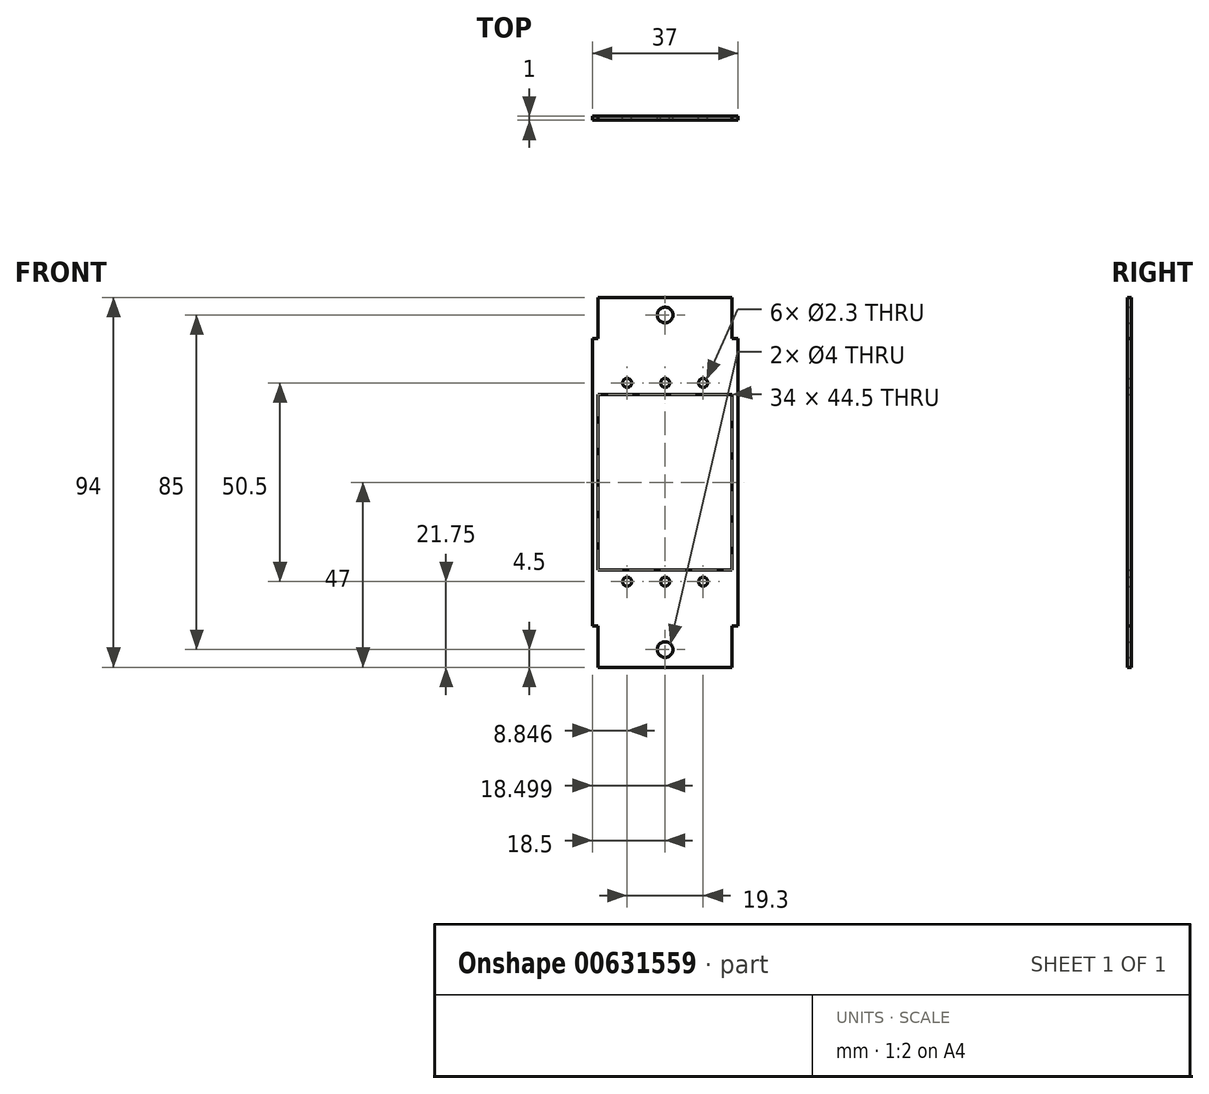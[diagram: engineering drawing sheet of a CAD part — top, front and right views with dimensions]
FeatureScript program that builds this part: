
annotation { "Feature Type Name" : "Feature", "Feature Type Description" : "" }
export const myFeature = defineFeature(function(context is Context, id is Id, definition is map)
    precondition{}
    {
        {
            var Q0;
            Q0=qCreatedBy(makeId("Front.planeOp"),FACE);
            var sketch = newSketch(context, id + "F0", { "sketchPlane" : qUnion([Q0])});
            skLineSegment(sketch, "E0.bottom", {"start": v(-17, 47) * mm, "end": v(17, 47) * mm});
            skLineSegment(sketch, "E0.top", {"start": v(-17, -47) * mm, "end": v(17, -47) * mm});
            skLineSegment(sketch, "E0.left", {"start": v(-18.5, 36.5) * mm, "end": v(-18.5, -36.5) * mm});
            skLineSegment(sketch, "E0.right", {"start": v(18.5, 36.5) * mm, "end": v(18.5, -36.5) * mm});
            skPoint(sketch, "E0.middle", {"position": v(0, 0) * mm});
            skLineSegment(sketch, "E1", {"start": v(17, 47) * mm, "end": v(17, 36.5) * mm});
            skLineSegment(sketch, "E2", {"start": v(17, 36.5) * mm, "end": v(18.5, 36.5) * mm});
            skLineSegment(sketch, "E3", {"start": v(-17, 47) * mm, "end": v(-17, 36.5) * mm});
            skLineSegment(sketch, "E4", {"start": v(-17, 36.5) * mm, "end": v(-18.5, 36.5) * mm});
            skPoint(sketch, "E5.orphan", {"position": v(18.5, 47) * mm});
            skLineSegment(sketch, "E6.MirrorCS", {"start": v(17, -36.5) * mm, "end": v(18.5, -36.5) * mm});
            skLineSegment(sketch, "E7.MirrorCS", {"start": v(17, -47) * mm, "end": v(17, -36.5) * mm});
            skLineSegment(sketch, "E8.MirrorCS", {"start": v(-17, -47) * mm, "end": v(-17, -36.5) * mm});
            skLineSegment(sketch, "E9.MirrorCS", {"start": v(-17, -36.5) * mm, "end": v(-18.5, -36.5) * mm});
            skCircle(sketch, "E10", {"center": v(0, 42.5) * mm, "radius": 2 * mm});
            skCircle(sketch, "E11.MirrorC", {"center": v(0, -42.5) * mm, "radius": 2 * mm});
            skLineSegment(sketch, "E12", {"start": v(0, -104.06) * mm, "end": v(0, 117.2) * mm, "construction": true});
            skCircle(sketch, "E13.MirrorC", {"center": v(9.65, -25.25) * mm, "radius": 1.15 * mm});
            skCircle(sketch, "E14.MirrorC", {"center": v(9.65, 25.25) * mm, "radius": 1.15 * mm});
            skCircle(sketch, "E15.MirrorC", {"center": v(-9.65, 25.25) * mm, "radius": 1.15 * mm});
            skCircle(sketch, "E16.MirrorC", {"center": v(0, -25.25) * mm, "radius": 1.15 * mm});
            skCircle(sketch, "E17.MirrorC", {"center": v(-9.65, -25.25) * mm, "radius": 1.15 * mm});
            skCircle(sketch, "E18.MirrorC", {"center": v(0, 25.25) * mm, "radius": 1.15 * mm});
            skLineSegment(sketch, "E19.MirrorCS", {"start": v(17, -22.25) * mm, "end": v(17, 22.25) * mm});
            skLineSegment(sketch, "E20.MirrorCS", {"start": v(-17, -22.25) * mm, "end": v(17, -22.25) * mm});
            skLineSegment(sketch, "E21.MirrorCS", {"start": v(-17, -22.25) * mm, "end": v(-17, 22.25) * mm});
            skLineSegment(sketch, "E22.MirrorCS", {"start": v(-17, 22.25) * mm, "end": v(17, 22.25) * mm});
            skSolve(sketch);
        }
        {
            var Q0;
            Q0=makeQuery(id+"F0.imprint","IMPRINT",FACE,{"disambiguationData":[TD([[makeQuery(id+"F0.imprint","IMPRINT",EDGE,{"derivedFrom":sQuery(id+"F0.wireOp",EDGE,"E0.bottom")}),-1.0]])]});
            extrude(context, id + "F1", {"entities" : qUnion([Q0]), "depth" : 1 * mm, "offsetDistance" : 25 * mm});
        }
    });
